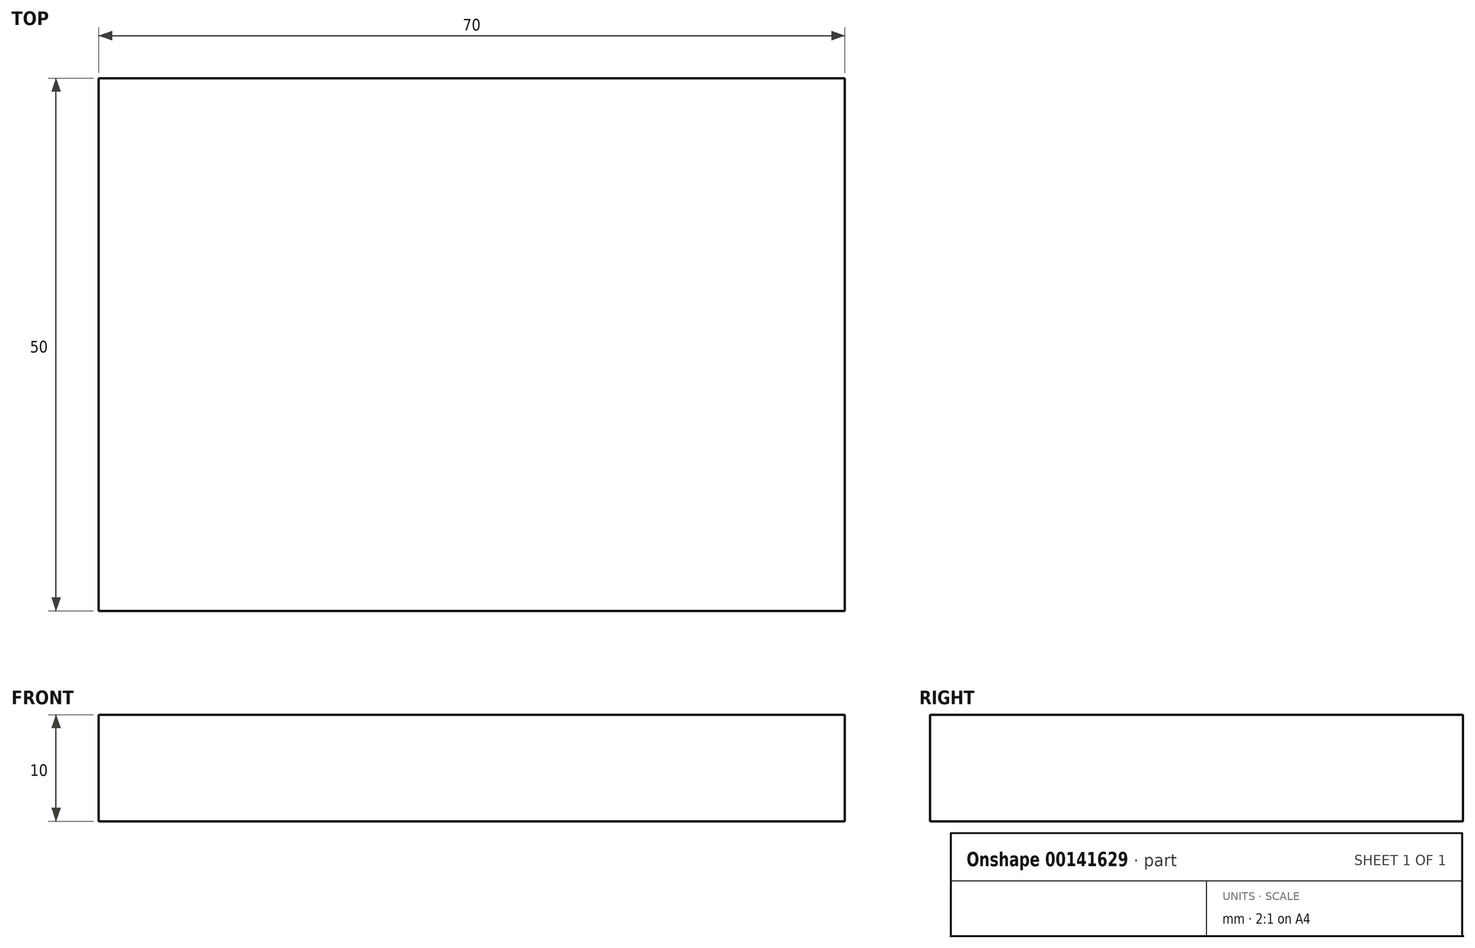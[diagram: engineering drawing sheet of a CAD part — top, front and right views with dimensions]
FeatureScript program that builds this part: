
annotation { "Feature Type Name" : "Feature", "Feature Type Description" : "" }
export const myFeature = defineFeature(function(context is Context, id is Id, definition is map)
    precondition{}
    {
        {
            var Q0;
            Q0=qCreatedBy(makeId("Top.planeOp"),FACE);
            var sketch = newSketch(context, id + "F0", { "sketchPlane" : qUnion([Q0])});
            skLineSegment(sketch, "E0.bottom", {"start": v(-20.62, 17.78) * mm, "end": v(49.38, 17.78) * mm});
            skLineSegment(sketch, "E0.top", {"start": v(-20.62, -32.22) * mm, "end": v(49.38, -32.22) * mm});
            skLineSegment(sketch, "E0.left", {"start": v(-20.62, 17.78) * mm, "end": v(-20.62, -32.22) * mm});
            skLineSegment(sketch, "E0.right", {"start": v(49.38, 17.78) * mm, "end": v(49.38, -32.22) * mm});
            skSolve(sketch);
        }
        {
            var Q0;
            Q0=makeQuery(id+"F0.imprint","IMPRINT",FACE,{"disambiguationData":[TD([[makeQuery(id+"F0.imprint","IMPRINT",EDGE,{"derivedFrom":sQuery(id+"F0.wireOp",EDGE,"E0.bottom")}),-1.0]])]});
            extrude(context, id + "F1", {"entities" : qUnion([Q0]), "depth" : 10 * mm});
        }
    });
